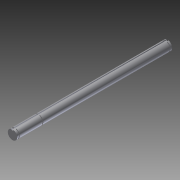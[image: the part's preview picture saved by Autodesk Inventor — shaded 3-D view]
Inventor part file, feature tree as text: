
AUTODESK INVENTOR PART (.ipt)
format: ipt  version: 2012 (Build 160160000, 160)  size: 112,640 bytes
history: native  units: in
note: dims shown in document units (in); Inventor stores cm internally (conversion verified against a paired STEP export)
features: extrude x4, sketch x4, plane x3, projected_geometry x1
ambient origin geometry x8: Origin, YZ Plane, XZ Plane, XY Plane, X Axis, Y Axis, Z Axis, Center Point
bodies: Solid1 (feature_tree)
feature tree (12):
  extrude  "Extrusion1"  Depth=6.1875in TaperAngle=0.0deg
  plane  "Work Plane1"
  extrude  "Extrusion2"  Depth=0.0787in
  plane  "Work Plane2"
  extrude  "Extrusion3"  Depth=0.1481in
  plane  "Work Plane3"
  extrude  "Extrusion4"  Depth=0.03in
  sketch  "Sketch1"  dims[d0=0.375in d1=6.1875in d2=0.0in]
  sketch  "Sketch2"  dims[d3=0.0787in d4=0.0787in]
  projected_geometry  "Projected Loop1"
  sketch  "Sketch3"  dims[d5=0.0394in d6=0.1481in]
  sketch  "Sketch4"  dims[d7=-0.0625in d9=0.03in d10=0.03in d11=0.0in d12=-5.145in d13=0.03in d14=0.0in d15=-0.0625in d16=0.04in d17=0.0in]
